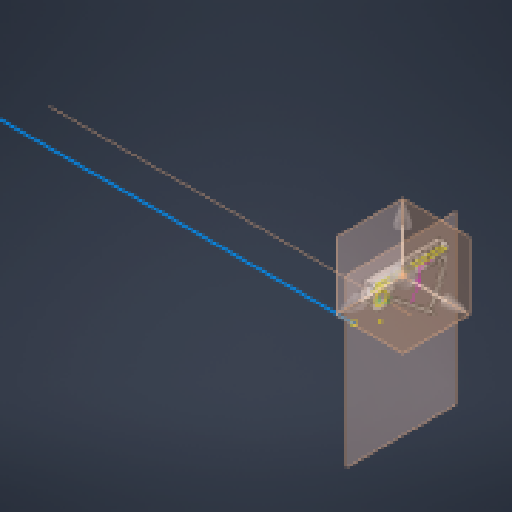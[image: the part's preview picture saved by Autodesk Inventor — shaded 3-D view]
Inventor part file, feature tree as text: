
AUTODESK INVENTOR PART (.ipt)
format: ipt  version: 2025 (Build 290162000, 162)  size: 445,440 bytes
history: native  units: mm
features: extrude x13, reference x12, other x10, sketch x9, projected_geometry x7, fillet x4, plane x1
ambient origin geometry x8: Origin, YZ Plane, XZ Plane, XY Plane, X Axis, Y Axis, Z Axis, Center Point
bodies: Solid1 (feature_tree)
feature tree (56):
  other  "Annotations"
  plane  "Work Plane1"
  extrude  "Thickness"  Depth=18.277605mm
  extrude  "sensor weight"  Depth=16.0mm
  extrude  "magnet mount and/or counterweight"  Depth=10.0mm
  extrude  "Extrusion4"  Depth=6.0mm
  extrude  "Extrusion5"  Depth=6.0mm
  extrude  "thin near bearing"  Depth=5.0mm TaperAngle=0.0deg
  extrude  "Extrusion7"  Depth=10.0mm
  extrude  "Extrusion8"  Depth=8.0mm
  extrude  "Extrusion9"  Depth=10.0mm TaperAngle=0.0deg
  extrude  "sensor flag"  Depth=10.0mm TaperAngle=0.0deg
  extrude  "sensor arm extension"  TaperAngle=0.0deg  [1 undecoded]
  extrude  "Extrusion12"  Depth=1.0mm
  extrude  "Extrusion13"  Depth=1.0mm
  fillet  "Fillet1"  Radius=16.0mm
  fillet  "Fillet2"  Radius=6.0mm
  fillet  "Fillet3"  Radius=8.0mm
  fillet  "Fillet4"  Radius=9.2mm
  other  "Work Axis1"
  sketch  "Sketch1"  dims[d0=102.0mm d1=18.277605mm]
  reference  "Reference1"
  reference  "Reference2"
  reference  "Reference3"
  reference  "Reference4"
  reference  "Reference5"
  reference  "Reference6"
  reference  "Reference7"
  projected_geometry  "Projected Loop1"
  projected_geometry  "Projected Loop2"
  sketch  "Sketch3"  dims[d4=99.0mm d5=10.0mm]
  sketch  "Sketch4"  dims[d6=10.200597mm d7=6.0mm]
  projected_geometry  "Projected Loop3"
  reference  "Reference8"
  reference  "Reference9"
  sketch  "Sketch5"  dims[d8=3.0mm d9=0.0mm d10=6.0mm]
  sketch  "Sketch Rectangular Pattern1"  dims[d2=16.0mm d3=16.0mm]
  sketch  "Sketch7"  dims[d11=3.0mm d12=0.0mm d17=5.0mm d18=0.0mm]
  projected_geometry  "Projected Loop4"
  sketch  "Sketch8"  dims[d19=2.9mm d20=60.0mm d22=5.0mm d23=10.0mm d25=10.0mm]
  projected_geometry  "Projected Loop5"
  reference  "Reference10"
  sketch  "Sketch12"  dims[d27=5.0mm d28=0.0mm d29=8.0mm]
  sketch  "Sketch13"  dims[d30=15.0mm d31=10.0mm d32=0.0mm d33=10.0mm d34=0.0mm d35=0.0mm d36=0.0mm d37=5.5mm d38=9.3mm d39=16.0mm d40=6.0mm d41=8.0mm d42=0.0mm d46=9.2mm d47=0.0mm d48=0.0mm d49=3.0mm d50=0.0mm d52=3.0mm d53=0.0mm d54=56.92138mm d55=115.904037mm d56=2.0mm d57=1.0mm d58=3.0mm d59=0.0mm d60=5.0mm d61=0.0mm d62=1.0mm d63=1.0mm d64=2.0mm d65=1.0mm d66=1.0mm d67=1.0mm d43=6.866406mm d44=4.220418mm d45=6.739106mm]
  projected_geometry  "Projected Loop6"
  reference  "Reference11"
  reference  "Reference12"
  projected_geometry  "Projected Loop7"
  other  "<userpath>\Desktop\rat basketball\rat_basketball\Hoop assembly\hoop assembly.iam"
  other  "hoop assembly.iam"
  other  "HOOP:1"
  other  "IR sensorIR Optical Sensor Module:1"
  other  "684AZZ:2"
  other  "684AZZ Outer Ring:1"
  other  "Angular Dimension 1"
  other  "Assembly1"
note: 1 required parameter value undecoded (feature->parameter linkage not recoverable at this tier; creation-order binding heuristic only, values carry confidence <= 0.55)
